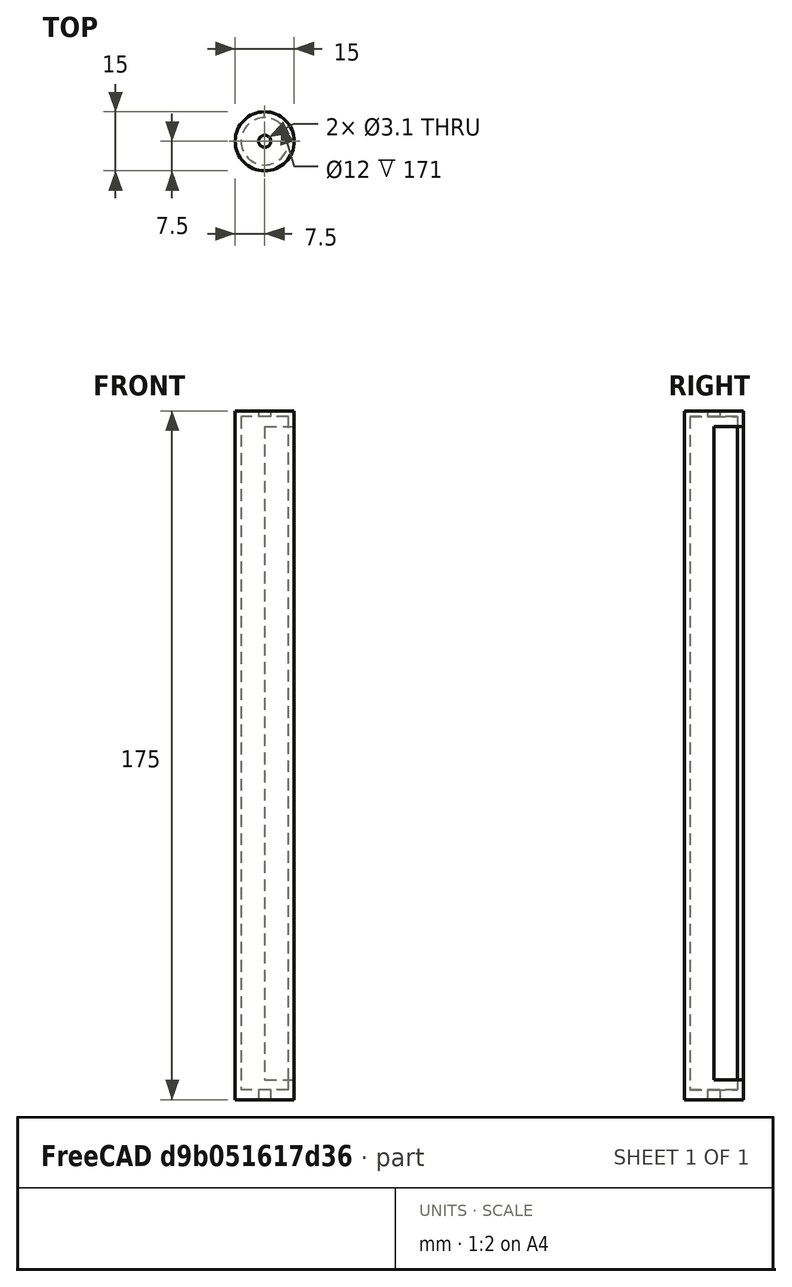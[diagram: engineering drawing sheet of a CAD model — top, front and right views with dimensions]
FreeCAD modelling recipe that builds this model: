
FCSTD DOCUMENT  (FreeCAD 1.0R39319 (Git))
Label: column_v1
License: Creative Commons Attribution-ShareAlike 4.0
LicenseURL: https://creativecommons.org/licenses/by-sa/4.0/
objects: PartDesign::SubtractiveCylinder×2, PartDesign::AdditiveCylinder×1, PartDesign::SubtractiveBox×1, PartDesign::Body×1, App::Part×1
note: 13 computed .brp shape members not serialized (recipe doc carries the construction recipe); baked Part::Feature solids carry a one-line shape summary decoded from their .brp

FEATURE [PartDesign::AdditiveCylinder] Cylinder
  Angle = 360
  AttacherType = Attacher::AttachEngine3D
  FirstAngle = 0
  Height = 175
  Radius = 7.5
  Refine = true
  SecondAngle = 0
  Suppressed = false
FEATURE [PartDesign::SubtractiveBox] Box
  AttacherType = Attacher::AttachEngine3D
  AttachmentOffset = pos=(0,0,5) rot=(0,0,1;0rad)
  AttachmentSupport = -> [XY_Plane]
  BaseFeature = -> Cylinder
  Height = 166
  Length = 10
  MapMode = 5
  Placement = pos=(0,0,5) rot=(0,0,1;0rad)
  Refine = true
  Suppressed = false
  Width = 10
FEATURE [PartDesign::SubtractiveCylinder] Cylinder001
  Angle = 360
  AttacherType = Attacher::AttachEngine3D
  AttachmentOffset = pos=(0,0,2.5) rot=(0,0,1;0rad)
  AttachmentSupport = -> [XY_Plane]
  BaseFeature = -> Box
  FirstAngle = 0
  Height = 171
  MapMode = 2
  Placement = pos=(0,0,2.5) rot=(0,0,1;0rad)
  Radius = 6
  Refine = true
  SecondAngle = 0
  Suppressed = false
FEATURE [PartDesign::SubtractiveCylinder] Cylinder002
  Angle = 360
  AttacherType = Attacher::AttachEngine3D
  BaseFeature = -> Cylinder001
  FirstAngle = 0
  Height = 175
  Radius = 1.55
  Refine = true
  SecondAngle = 0
  Suppressed = false
FEATURE [PartDesign::Body] Body
  AllowCompound = false
  Group = -> [Cylinder,Box,Cylinder001,Cylinder002]
  Origin = -> Origin
  Tip = -> Cylinder002
FEATURE [App::Part] Part  label="Column"
  Group = -> [Body]
  Origin = -> Origin001
